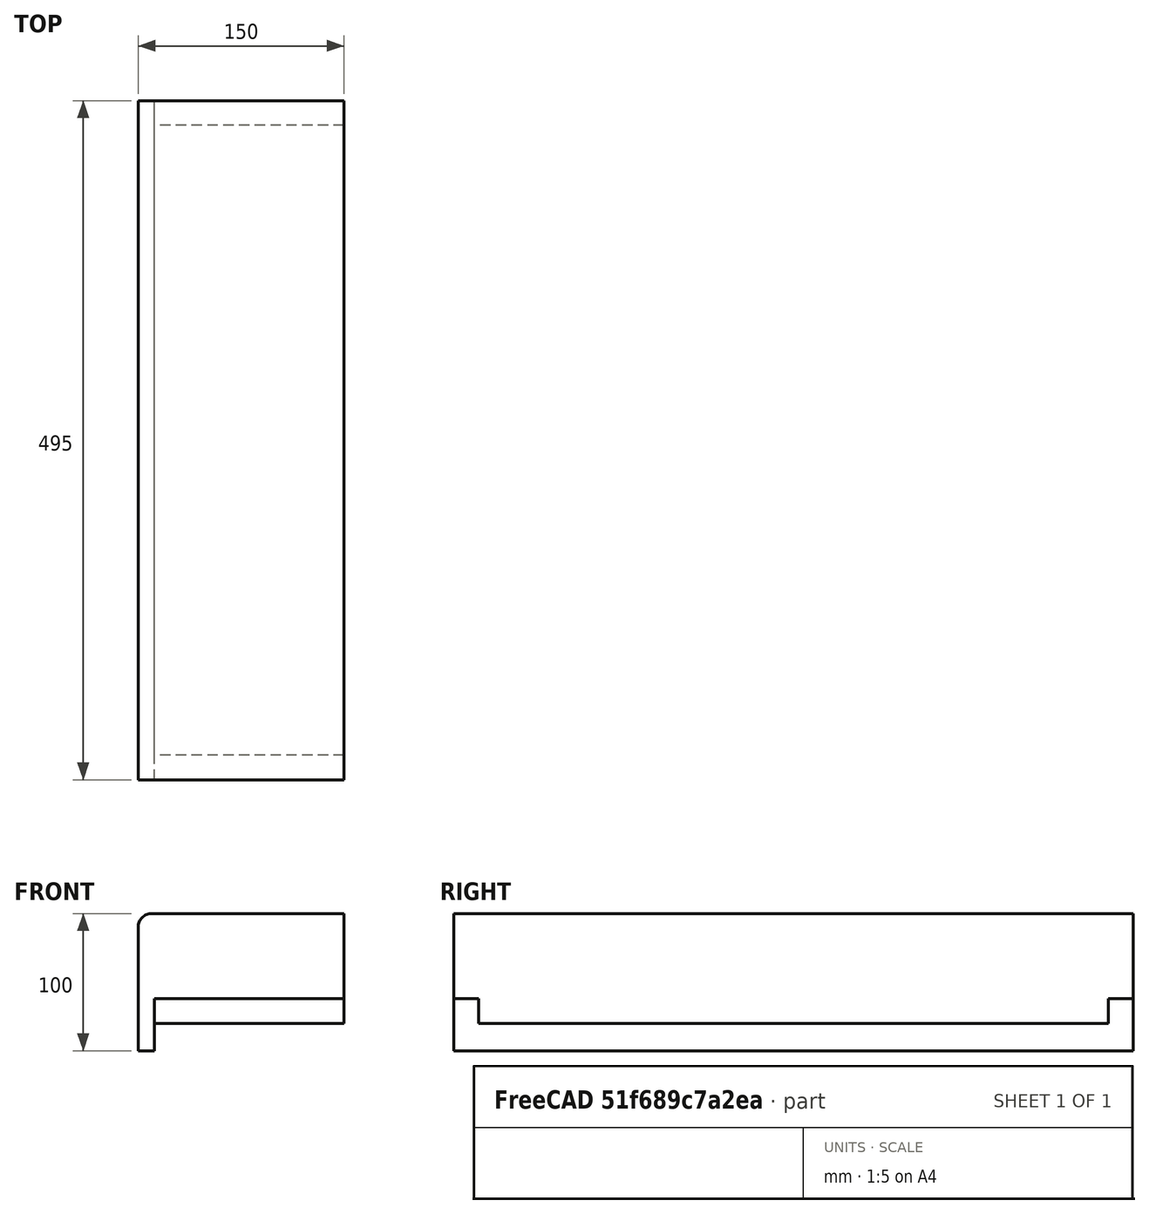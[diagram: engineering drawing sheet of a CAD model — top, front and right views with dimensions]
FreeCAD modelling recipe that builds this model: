
FCSTD DOCUMENT  (FreeCAD 0.19R24276 (Git))
Label: 1001_keyboard_Shrimpwrap_
License: All rights reserved
LicenseURL: http://en.wikipedia.org/wiki/All_rights_reserved
objects: TechDraw::DrawViewDimension×7, Sketcher::SketchObject×2, TechDraw::DrawSVGTemplate×2, TechDraw::DrawPage×2, TechDraw::DrawViewPart×2, PartDesign::Pad×1, Spreadsheet::Sheet×1, PartDesign::Pocket×1, PartDesign::Fillet×1, PartDesign::Body×1
note: 9 computed .brp shape members not serialized (recipe doc carries the construction recipe); baked Part::Feature solids carry a one-line shape summary decoded from their .brp

FEATURE [Sketcher::SketchObject] Sketch  label="SideWall"
  FullyConstrained = true
  MapMode = 5
  Placement = pos=(0,0,0) rot=(1,0,0;1.5708rad)
  Support = -> [XZ_Plane]
  sketch-geometry (6):
    g0: LineSegment StartX=138 StartY=0 StartZ=0 EndX=0 EndY=0 EndZ=0
    g1: LineSegment StartX=-12 StartY=80 StartZ=0 EndX=138 EndY=80 EndZ=0
    g2: LineSegment StartX=138 StartY=80 StartZ=0 EndX=138 EndY=0 EndZ=0
    g3: LineSegment StartX=-12 StartY=80 StartZ=0 EndX=-12 EndY=-20 EndZ=0
    g4: LineSegment StartX=-12 StartY=-20 StartZ=0 EndX=0 EndY=-20 EndZ=0
    g5: LineSegment StartX=0 StartY=-20 StartZ=0 EndX=0 EndY=0 EndZ=0
  constraints (18):
    c: Coincident(g0,g-1)
    c: Horizontal(g0)
    c: Vertical(g2)
    c: Coincident(g0,g2)
    c: Coincident(g2,g1)
    c: Vertical(g3)
    c: Coincident(g4,g3)
    c: PointOnObject(g4,g-2)
    c: Horizontal(g4)
    c: Coincident(g5,g4)
    c: Coincident(g5,g0)
    c: Coincident(g3,g1)
    c: Horizontal(g1)
    c: DistanceX(g4,g4) = 12
    c: DistanceY(g3,g3) = 100
    c: DistanceX(g1,g1) = 150
    c: DistanceY(g5,g5) = 20
    c: DistanceY(g2,g2) = 80
FEATURE [PartDesign::Pad] Pad
  AllowMultiFace = false
  Direction = (1,1,1)
  Length = 495
  Length2 = 13
  Placement = pos=(0,0,0) rot=(1,0,0;1.5708rad)
  Profile = -> Sketch
  Reversed = true
  Type = 0
FEATURE [Spreadsheet::Sheet] Spreadsheet  label="xls"
  cells = C2=INHERITED DIMENSIONS; C3=Thickness; D3=kbf_t_0; E3=16; F3=mm; H3=NOTE: No plexi; C5=SIDEWALL ; C6=thickness of board; D6=t; E6(nt)=16; F6=mm; C7=Depth of Board; E7=150; G7=NOMINAL; C8=Depth of board; D8=X0; E8(X0)==+E7 - E3; F8=mm; G8=REAL; C9=Height of board; D9=Z0; E9(z_0)=100; F9=mm
FEATURE [Sketcher::SketchObject] Sketch001
  ExternalGeometry = -> [Pad]
  FullyConstrained = true
  MapMode = 5
  Placement = pos=(138,0,0) rot=(0.707107,0,0.707107;3.14159rad)
  Support = -> [Pad]
  sketch-geometry (8):
    g0: LineSegment StartX=18 StartY=0 StartZ=0 EndX=0 EndY=0 EndZ=0
    g1: LineSegment StartX=0 StartY=0 StartZ=0 EndX=0 EndY=-18 EndZ=0
    g2: LineSegment StartX=0 StartY=-18 StartZ=0 EndX=18 EndY=-18 EndZ=0
    g3: LineSegment StartX=18 StartY=-18 StartZ=0 EndX=18 EndY=0 EndZ=0
    g4: LineSegment StartX=0 StartY=-495 StartZ=0 EndX=18 EndY=-495 EndZ=0
    g5: LineSegment StartX=18 StartY=-495 StartZ=0 EndX=18 EndY=-477 EndZ=0
    g6: LineSegment StartX=18 StartY=-477 StartZ=0 EndX=0 EndY=-477 EndZ=0
    g7: LineSegment StartX=0 StartY=-477 StartZ=0 EndX=0 EndY=-495 EndZ=0
  constraints (22):
    c: PointOnObject(g0,g-3)
    c: Coincident(g0,g-1)
    c: Coincident(g1,g0)
    c: PointOnObject(g1,g-2)
    c: Coincident(g2,g1)
    c: Horizontal(g2)
    c: Coincident(g3,g2)
    c: Coincident(g3,g0)
    c: Vertical(g3)
    c: DistanceY(g3,g3) = 18
    c: Equal(g3,g2)
    c: Coincident(g4,g-4)
    c: Horizontal(g4)
    c: Coincident(g5,g4)
    c: Vertical(g5)
    c: Coincident(g6,g5)
    c: Horizontal(g6)
    c: Coincident(g7,g6)
    c: Coincident(g7,g4)
    c: Vertical(g7)
    c: Equal(g6,g5)
    c: Equal(g6,g2)
FEATURE [PartDesign::Pocket] Pocket
  BaseFeature = -> Pad
  Length = 0
  Length2 = 100
  Placement = pos=(0,0,0) rot=(1,0,0;1.5708rad)
  Profile = -> Sketch001
  Type = 3
  UpToFace = -> Pad [Face4]
FEATURE [PartDesign::Fillet] Fillet
  Base = -> Pocket [Edge1]
  BaseFeature = -> Pocket
  Placement = pos=(0,0,0) rot=(1,0,0;1.5708rad)
  Radius = 10
  SupportTransform = false
FEATURE [PartDesign::Body] Body
  Group = -> [Sketch,Pad,Sketch001,Pocket,Fillet]
  Origin = -> Origin
  Tip = -> Fillet
FEATURE [TechDraw::DrawSVGTemplate] Template
  EditableTexts = Designed_by_Name=Designed by Name; Drawing_number=Drawing number; FC-Date=Date; FC-SC=Scale; FC-SH=Sheet; FC-Title=Title; Subtitle=Subtitle; Weight=Weight
  Height = 210
  Orientation = 1
  Width = 297
FEATURE [TechDraw::DrawPage] Page
  KeepUpdated = true
  NextBalloonIndex = 1
  ProjectionType = 0
  Template = -> Template
FEATURE [TechDraw::DrawSVGTemplate] Template001
  EditableTexts = Designed_by_Name=Designed by Name; Drawing_number=Drawing number; FC-Date=Date; FC-SC=Scale; FC-SH=Sheet; FC-Title=Title; Subtitle=Subtitle; Weight=Weight
  Height = 210
  Orientation = 1
  Width = 297
FEATURE [TechDraw::DrawViewPart] View
  CoarseView = false
  Direction = (0,1,0)
  Focus = 100
  HardHidden = false
  IsoCount = 0
  IsoHidden = false
  IsoVisible = false
  LockPosition = false
  Perspective = false
  Rotation = 0
  Scale = 0.5
  ScaleType = 2
  SeamHidden = false
  SeamVisible = true
  SmoothHidden = false
  SmoothVisible = true
  Source = -> [Fillet]
  X = 85.2462
  XDirection = (1,0,0)
  Y = 49.1648
FEATURE [TechDraw::DrawViewDimension] Dimension
  Arbitrary = false
  ArbitraryTolerances = false
  EqualTolerance = true
  FormatSpec = %.2f
  FormatSpecOverTolerance = %+.2f
  FormatSpecUnderTolerance = %+.2f
  Inverted = false
  LockPosition = false
  MeasureType = 1
  OverTolerance = 0
  References2D = -> [View]
  Rotation = 0
  ScaleType = 0
  TheoreticalExact = false
  Type = 2
  UnderTolerance = 0
  X = 43.7635
  Y = -10.3905
FEATURE [TechDraw::DrawViewDimension] Dimension001
  Arbitrary = false
  ArbitraryTolerances = false
  EqualTolerance = true
  FormatSpec = %.2f
  FormatSpecOverTolerance = %+.2f
  FormatSpecUnderTolerance = %+.2f
  Inverted = false
  LockPosition = false
  MeasureType = 1
  OverTolerance = 0
  References2D = -> [View]
  Rotation = 0
  ScaleType = 0
  TheoreticalExact = false
  Type = 2
  UnderTolerance = 0
  X = -15.3644
  Y = -5.55099
FEATURE [TechDraw::DrawViewDimension] Dimension002
  Arbitrary = false
  ArbitraryTolerances = false
  EqualTolerance = true
  FormatSpec = %.2f
  FormatSpecOverTolerance = %+.2f
  FormatSpecUnderTolerance = %+.2f
  Inverted = false
  LockPosition = false
  MeasureType = 1
  OverTolerance = 0
  References2D = -> [View]
  Rotation = 0
  ScaleType = 0
  TheoreticalExact = false
  Type = 1
  UnderTolerance = 0
  X = 10.4664
  Y = -11.3449
FEATURE [TechDraw::DrawViewDimension] Dimension003
  Arbitrary = false
  ArbitraryTolerances = false
  EqualTolerance = true
  FormatSpec = %.2f
  FormatSpecOverTolerance = %+.2f
  FormatSpecUnderTolerance = %+.2f
  Inverted = false
  LockPosition = false
  MeasureType = 1
  OverTolerance = 0
  References2D = -> [View]
  Rotation = 0
  ScaleType = 0
  TheoreticalExact = false
  Type = 2
  UnderTolerance = 0
  X = -59.3818
  Y = 1.87635
FEATURE [TechDraw::DrawViewDimension] Dimension004
  Arbitrary = false
  ArbitraryTolerances = false
  EqualTolerance = true
  FormatSpec = %.2f
  FormatSpecOverTolerance = %+.2f
  FormatSpecUnderTolerance = %+.2f
  Inverted = false
  LockPosition = false
  MeasureType = 1
  OverTolerance = 0
  References2D = -> [View]
  Rotation = 0
  ScaleType = 0
  TheoreticalExact = false
  Type = 1
  UnderTolerance = 0
  X = -22.0054
  Y = 35.9328
FEATURE [TechDraw::DrawViewPart] View001
  CoarseView = false
  Direction = (-1,0,0)
  Focus = 100
  HardHidden = false
  IsoCount = 0
  IsoHidden = false
  IsoVisible = false
  LockPosition = false
  Perspective = false
  Rotation = 0
  Scale = 0.5
  ScaleType = 0
  SeamHidden = false
  SeamVisible = true
  SmoothHidden = false
  SmoothVisible = true
  Source = -> [Fillet]
  X = 148.89
  XDirection = (0,-1,0)
  Y = 147.169
FEATURE [TechDraw::DrawViewDimension] Dimension005
  Arbitrary = false
  ArbitraryTolerances = false
  EqualTolerance = true
  FormatSpec = %.2f
  FormatSpecOverTolerance = %+.2f
  FormatSpecUnderTolerance = %+.2f
  Inverted = false
  LockPosition = false
  MeasureType = 1
  OverTolerance = 0
  References2D = -> [View001]
  Rotation = 0
  ScaleType = 0
  TheoreticalExact = false
  Type = 1
  UnderTolerance = 0
  X = 1.95228
  Y = 37.4946
FEATURE [TechDraw::DrawViewDimension] Dimension006
  Arbitrary = false
  ArbitraryTolerances = false
  EqualTolerance = true
  FormatSpec = %.2f
  FormatSpecOverTolerance = %+.2f
  FormatSpecUnderTolerance = %+.2f
  Inverted = false
  LockPosition = false
  MeasureType = 1
  OverTolerance = 0
  References2D = -> [View001]
  Rotation = 0
  ScaleType = 0
  TheoreticalExact = false
  Type = 2
  UnderTolerance = 0
  X = 131.559
  Y = 1.56182
FEATURE [TechDraw::DrawPage] Page001
  KeepUpdated = true
  NextBalloonIndex = 1
  ProjectionType = 0
  Template = -> Template001
  Views = -> [View,Dimension,Dimension001,Dimension002,Dimension003,Dimension004,View001,Dimension005,Dimension006]
